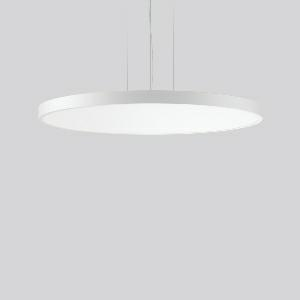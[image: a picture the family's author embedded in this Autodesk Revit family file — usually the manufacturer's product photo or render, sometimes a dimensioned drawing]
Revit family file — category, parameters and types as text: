
# Revit family: triona_round_p_312393_002_730_e77c
name_source: partatom
category: Lighting Fixtures
units: mm (PartAtom-declared; Revit-internal decimal feet)

## family parameters
Cut with Voids When Loaded = No
Host = Face
Light Source = No
Part Type = Normal
Room Calculation Point = No
Round Connector Dimension = Use Diameter
Shared = No

## types (1)
- TRIONA round P (1 x LED Modul 830, 11200 lm, 3000)
    Apparent Load = 106 VA
    CIE Flux Codes = 49 80 96 100 100
    Color Rendering = 80
    Color Temperature = 3000
    Default Elevation = 1800 mm
    Description = Series: TRIONA round
Decorative round LED pendant-mounted surface luminaire. Flat, seamless frame: aluminium extrusion profile, powder coated. Cover made of sheet steel, powder-coated. Canopy made of aluminium, powder-coated. Light emission through a diffuser: plastic, opal. Lightguide and diffuser made of non-yellowing plastic (PMMA). Lateral light emission (RZB SIDELITE technology) for above-average homogeneous light distribution. 3-point steel cable suspension, steplessly adjustable. Easy installation with transparent, adjustable pendant cable and canopy with magnetic fixing. Driver integrated. 
Colour: traffic white, matt (RAL 9016)
Diameter: 1009 mm
Height: 52 mm
Suspension length: 500-1200 mm
Lamp: LED
Socket: without socket
Colour temperature: 3000K
Colour rendering index (CRI): 80
System power: 106 W
Rated luminous flux: 11200 lm
Luminous efficiency: 106 lm/W
Control gear: Dimmable Bluetooth converter
Protection class: I
Type of protection: IP 20
    Height = 52 mm  [stored 0.170604 ft]
    Lamp = 1 x LED Modul 830
    Lamp Light Flux = 11200 lm
    Lamp count = 1
    Length = 1009 mm
    Lifetime = 50000 h
    Luminous efficacy = 106 lm/W
    Manufacturer = RZB
    ModVariant = No
    Model = 312393.002.730
    Mounting Place = Ceiling
    Mounting Type = Pendant
    Number of Poles = 1
    OnlyDefault = Yes
    Power Factor = 1
    Product Name = TRIONA round P
    Product group = Pendant modular luminaires
    ProductGroupID = 906
    Protection Class = Protection class I
    Protection Degree = IP 20
    RLX_Detail_Level = 1
    RLX_Emergency_Light_Flux = 0 lm
    RLX_Emergency_Type = 0
    RLX_Emergency_Type_DB = No
    RlxData = <blob elided: 29305 chars, md5=2f748cf4>
    Socket = socket
    Standby Power = 0 W
    System Light Flux = 11200 lm
    System Power = 106 W
    Type Comments = Product without accessories
    Type Image = 312394.002.jpg
    URL = http://relux.com
    VarID = ---
    Voltage = 230 V
    Voltage Range = 220-240 V
    Weight = 0.00 kg
    Width = 0 mm  [stored 0 ft]

note: [stored X ft] marks values corroborated as IEEE doubles in the binary element streams (Revit-internal decimal feet)

## geometry (parser evidence)
native form markers: Blend x4, Sweep x10
no freeform markers — native parametric forms only
